# Revit family: Gleitlager T ohne Schalldämmung, Ø64 - Ø219mm
name_source: partatom
category: HLS-Bauteile
units: mm (PartAtom-declared; Revit-internal decimal feet)

## family parameters
Arbeitsebenenbasiert = Ja
Beim Laden mit Abzugskörper schneiden = Nein
Bemaßung runder Anschluss = Durchmesser verwenden
Beschriftungsausrichtung beibehalten = Nein
Gemeinsam genutzt = Ja
Immer vertikal = Nein
Klassifizierung = Keine
Raumberechnungspunkt = Nein
Teiletyp = Normal

## types (13) — shared parameters
Breite Schellenband = 50 mm
Breite Unterbau = 100 mm
Fabrikat = MEFA
Höhe Unterbau = 105 mm
Kurztext1 = Gleitlager T h=105 50 x 5 mm
Länge Unterbau = 250 mm
Material = Stahl
Materialname = S235
Mengeneinheit = St
Schalldämmeinlage = ohne Dämmung
Sicherheitsfaktor = 1.54
Stärke Schellenband = 5 mm
Verschluss-Schraube = M12
Vorgabe-Ansicht = 1219 mm
vpe = 1
zero-valued in all types: Dämmstärke, Stärke, max. Rohraußendurchmesser, min. Rohraußendurchmesser

## per-type parameters (varying)
| type | Artikelnummer | EAN | Gewicht | Gewicht pro Bauteil | Hersteller | Kurztext2 | Nennweite DN Rohr | RS Titan Ø64 bis Ø219 | Rohraußendurchmesser |
| Gleitlager T Ø 108, o.Däm. | 145fa0108 | 4250928459930 | 6.74 kg | 6.74 kg |  | 108 mm o. Dämm. fsv | 0 mm  [stored 0 ft] | Rohrschelle Titan HD, o.A, o.D, 30Grad : Titan HD, o.A., Ø108mm | 108 mm  [stored 0.354331 ft] |
| Gleitlager T Ø  89, o.Däm. | 145fa0089 | 4250928459923 | 6.48 kg | 6.48 kg |  | 89 mm o. Dämm. fsv | 80 mm  [stored 0.262467 ft] | Rohrschelle Titan HD, o.A, o.D, 30Grad : Titan HD, o.A., Ø89mm | 89 mm  [stored 0.291995 ft] |
| Gleitlager T Ø  76, o.Däm. | 145fa0076 | 4250928459916 | 6.29 kg | 6.29 kg | MEFA | 76 mm o. Dämm. fsv | 65 mm  [stored 0.213255 ft] | Rohrschelle Titan HD, o.A, o.D, 30Grad : Titan HD, o.A., Ø76mm | 76 mm  [stored 0.249344 ft] |
| Gleitlager T Ø  64, o.Däm. | 145fa0064 | 4250928459909 | 6.13 kg | 6.13 kg | MEFA | 64 mm o. Dämm. fsv | 0 mm  [stored 0 ft] | Rohrschelle Titan HD, o.A, o.D, 30Grad : Titan HD, o.A., Ø64mm | 64 mm  [stored 0.209974 ft] |
| Gleitlager T Ø 110, o.Däm. | 145fa0110 | 4250928459947 | 6.77 kg | 6.77 kg |  | 110 mm o. Dämm. fsv | 0 mm  [stored 0 ft] | Rohrschelle Titan HD, o.A, o.D, 30Grad : Titan HD, o.A., Ø110mm | 110 mm  [stored 0.360892 ft] |
| Gleitlager T Ø 114, o.Däm. | 145fa0114 | 4250928459954 | 6.83 kg | 6.83 kg |  | 114 mm o. Dämm. fsv | 100 mm  [stored 0.328084 ft] | Rohrschelle Titan HD, o.A, o.D, 30Grad : Titan HD, o.A., Ø114mm | 114 mm  [stored 0.374016 ft] |
| Gleitlager T Ø 133, o.Däm. | 145fa0133 | 4250928459961 | 7.09 kg | 7.09 kg |  | 133 mm o. Dämm. fsv | 0 mm  [stored 0 ft] | Rohrschelle Titan HD, o.A, o.D, 30Grad : Titan HD, o.A., Ø133mm | 133 mm  [stored 0.436352 ft] |
| Gleitlager T Ø 140, o.Däm. | 145fa0140 | 4250928459978 | 7.19 kg | 7.19 kg |  | 140 mm o. Dämm. fsv | 125 mm  [stored 0.410105 ft] | Rohrschelle Titan HD, o.A, o.D, 30Grad : Titan HD, o.A., Ø140mm | 140 mm  [stored 0.459318 ft] |
| Gleitlager T Ø 160, o.Däm. | 145fa0160 | 4250928459985 | 7.47 kg | 7.47 kg |  | 160 mm o. Dämm. fsv | 0 mm  [stored 0 ft] | Rohrschelle Titan HD, o.A, o.D, 30Grad : Titan HD, o.A., Ø160mm | 160 mm  [stored 0.524934 ft] |
| Gleitlager T Ø 168, o.Däm. | 145fa0168 | 4250928459992 | 7.58 kg | 7.58 kg |  | 168 mm o. Dämm. fsv | 150 mm | Rohrschelle Titan HD, o.A, o.D, 30Grad : Titan HD, o.A., Ø168mm | 168 mm  [stored 0.551181 ft] |
| Gleitlager T Ø 180, o.Däm. | 145fa0180 | 4250928460004 | 7.74 kg | 7.74 kg |  | 180 mm o. Dämm. fsv | 0 mm  [stored 0 ft] | Rohrschelle Titan HD, o.A, o.D, 30Grad : Titan HD, o.A., Ø180mm | 180 mm  [stored 0.590551 ft] |
| Gleitlager T Ø 210, o.Däm. | 145fa0210 | 4250928460011 | 8.16 kg | 8.16 kg |  | 210 mm o. Dämm. fsv | 0 mm  [stored 0 ft] | Rohrschelle Titan HD, o.A, o.D, 30Grad : Titan HD, o.A., Ø210mm | 210 mm  [stored 0.688976 ft] |
| Gleitlager T Ø 219, o.Däm. | 145fa0219 | 4250928460028 | 8.29 kg | 8.29 kg |  | 219 mm o. Dämm. fsv | 200 mm  [stored 0.656168 ft] | Rohrschelle Titan HD, o.A, o.D, 30Grad : Titan HD, o.A., Ø219mm | 219 mm  [stored 0.718504 ft] |

note: [stored X ft] marks values corroborated as IEEE doubles in the binary element streams (Revit-internal decimal feet)

## geometry (parser evidence)
native form markers: Sweep x6
no freeform markers — native parametric forms only
